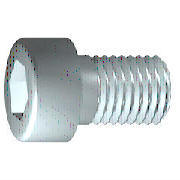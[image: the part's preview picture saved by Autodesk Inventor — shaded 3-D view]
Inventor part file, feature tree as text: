
AUTODESK INVENTOR PART (.ipt)
format: ipt  version: 2013 (Build 170138000, 138)  size: 184,832 bytes
history: native  units: mm (DEFAULTED — no unit token found)
features: sketch x2, extrude x1, plane x1, fillet x1
ambient origin geometry x7: Origin, YZ Plane, XY Plane, X Axis, Y Axis, Z Axis, Center Point
bodies: Solid1 (feature_tree), Body (feature_tree)
feature tree (5):
  extrude  "Slot"  Depth=0.306825mm
  plane  "Work Plane1"
  fillet  "Fillet2"  Radius=3.0mm
  sketch  "Sketch1"  dims[d1=14.693275mm d2=0.306825mm d3=3.0mm]
  sketch  "Sketch2"  dims[d4=1.5mm d5=60.0deg d6=3.0mm d7=3.0mm d8=2.886751mm d9=5.5mm d10=90.0deg d11=10.0mm d12=0.0mm d13=14.693275mm d14=0.0mm d15=0.306725mm d16=0.306725mm d17=0.3mm d19=0.0mm d26=16.0mm d27=45.0deg d28=0.0mm d29=0.0mm d30=0.1mm]
